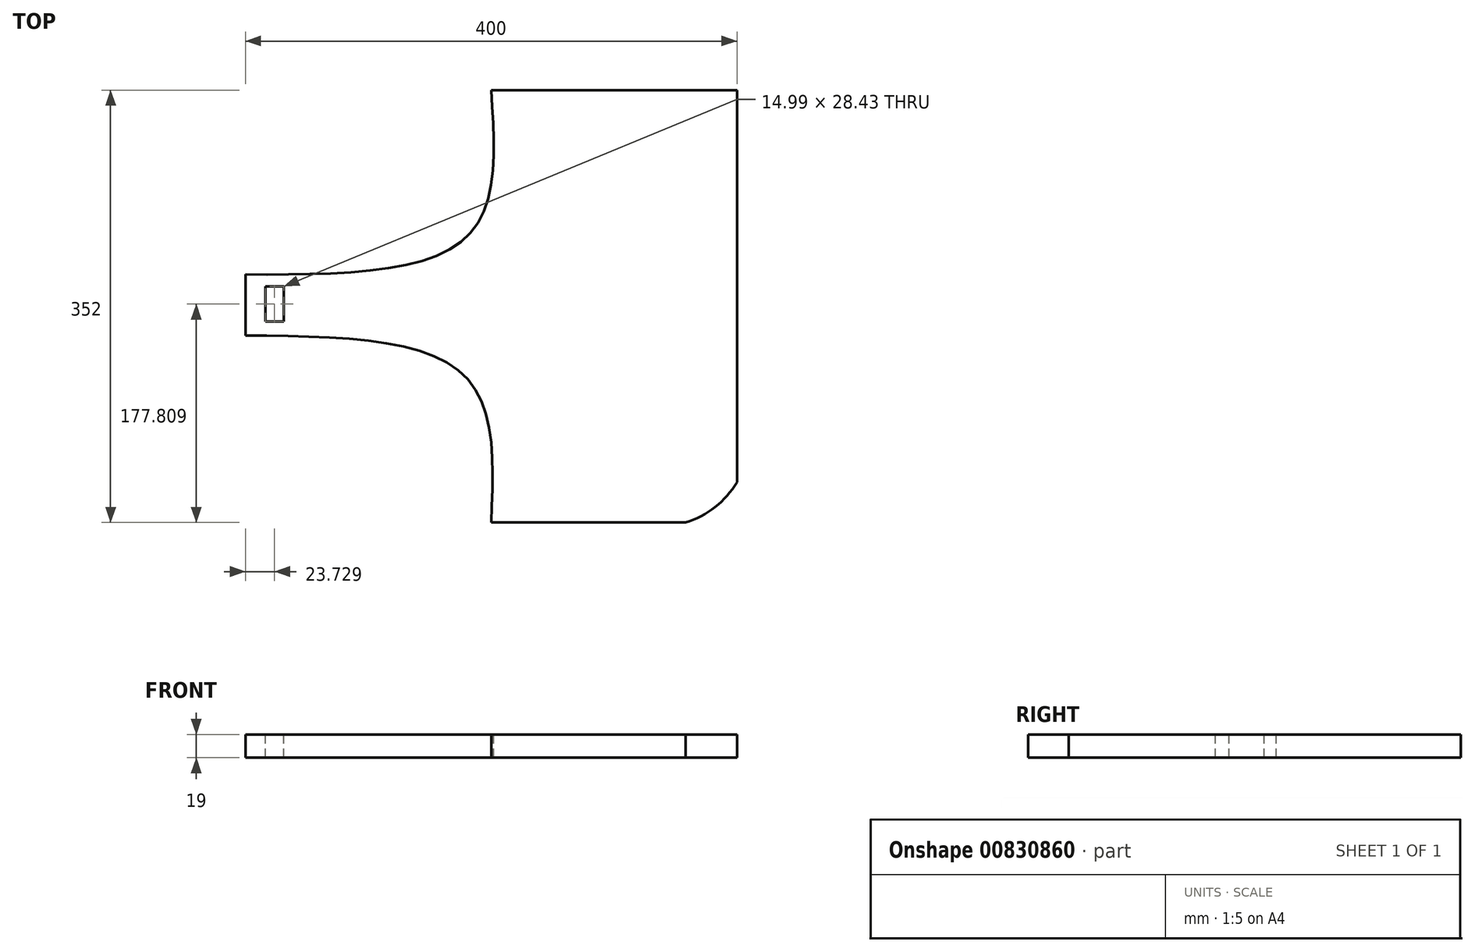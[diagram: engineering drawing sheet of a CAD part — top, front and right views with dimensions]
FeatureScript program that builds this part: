
annotation { "Feature Type Name" : "Feature", "Feature Type Description" : "" }
export const myFeature = defineFeature(function(context is Context, id is Id, definition is map)
    precondition{}
    {
        {
            var Q0;
            Q0=qCreatedBy(makeId("Top.planeOp"),FACE);
            var sketch = newSketch(context, id + "F0", { "sketchPlane" : qUnion([Q0])});
            skLineSegment(sketch, "E0.bottom", {"start": v(200, -176) * mm, "end": v(-200, -176) * mm});
            skLineSegment(sketch, "E0.top", {"start": v(200, 176) * mm, "end": v(-200, 176) * mm});
            skLineSegment(sketch, "E0.left", {"start": v(200, -176) * mm, "end": v(200, 176) * mm});
            skLineSegment(sketch, "E0.right", {"start": v(-200, -176) * mm, "end": v(-200, 176) * mm});
            skPoint(sketch, "E0.middle", {"position": v(0, 0) * mm});
            skSolve(sketch);
        }
        {
            var Q0;
            Q0=makeQuery(id+"F0.imprint","IMPRINT",FACE,{"disambiguationData":[TD([[makeQuery(id+"F0.imprint","IMPRINT",EDGE,{"derivedFrom":sQuery(id+"F0.wireOp",EDGE,"E0.bottom")}),-1.0]])]});
            extrude(context, id + "F1", {"entities" : qUnion([Q0]), "depth" : 19 * mm, "offsetDistance" : 25 * mm});
        }
        {
            var Q0;
            Q0=makeQuery(id+"F1.opExtrude","CAP_FACE",FACE,{"disambiguationData":[OSD([sQuery(id+"F0.wireOp",EDGE,"E0.bottom"),sQuery(id+"F0.wireOp",EDGE,"E0.top"),sQuery(id+"F0.wireOp",EDGE,"E0.left"),sQuery(id+"F0.wireOp",EDGE,"E0.right")])],"isStart":false});
            var sketch = newSketch(context, id + "F2", { "sketchPlane" : qUnion([Q0])});
            skFitSpline(sketch, "E1", {"points": [v(-200, -23.78) * mm, v(-21.45, -56.86) * mm, v(0, -176) * mm], "startDerivative": vector(400.47, -3.68) * mm, "endDerivative": vector(-14.44, -311.12) * mm});
            skFitSpline(sketch, "E2", {"points": [v(-200, 25.85) * mm, v(-18.87, 57.38) * mm, v(0, 176) * mm], "startDerivative": vector(406.43, -0.6) * mm, "endDerivative": vector(-21.56, 311.95) * mm});
            skLineSegment(sketch, "E3.bottom", {"start": v(-177.27, 14.17) * mm, "end": v(-156.69, 14.17) * mm});
            skLineSegment(sketch, "E3.top", {"start": v(-177.27, -14.17) * mm, "end": v(-156.69, -14.17) * mm});
            skLineSegment(sketch, "E3.left", {"start": v(-177.27, 14.17) * mm, "end": v(-177.27, -14.17) * mm});
            skLineSegment(sketch, "E3.right", {"start": v(-156.69, 14.17) * mm, "end": v(-156.69, -14.17) * mm});
            skPoint(sketch, "E3.middle", {"position": v(-166.98, 0) * mm});
            skSolve(sketch);
        }
        {
            var Q0;
            {var subQ0=sQuery(id+"F2.wireOp",EDGE,"E1");Q0=makeQuery(id+"F2.imprint","IMPRINT",FACE,{"disambiguationData":[TD([[makeQuery(id+"F2.imprint","IMPRINT",EDGE,{"derivedFrom":subQ0}),-1.0]])]});}
            var Q1;
            {var subQ0=sQuery(id+"F2.wireOp",EDGE,"E2");Q1=makeQuery(id+"F2.imprint","IMPRINT",FACE,{"disambiguationData":[TD([[makeQuery(id+"F2.imprint","IMPRINT",EDGE,{"derivedFrom":subQ0}),1.0]])]});}
            extrude(context, id + "F3", {"entities" : qUnion([Q0, Q1]), "operationType" : NewBodyOperationType.REMOVE, "endBound" : BoundingType.THROUGH_ALL, "oppositeDirection" : true, "depth" : 25 * mm, "offsetDistance" : 25 * mm});
        }
        {
            var Q0;
            Q0=makeQuery(id+"F1.opExtrude","CAP_FACE",FACE,{"disambiguationData":[OSD([sQuery(id+"F0.wireOp",EDGE,"E0.bottom"),sQuery(id+"F0.wireOp",EDGE,"E0.top"),sQuery(id+"F0.wireOp",EDGE,"E0.left"),sQuery(id+"F0.wireOp",EDGE,"E0.right")])],"isStart":false});
            var sketch = newSketch(context, id + "F4", { "sketchPlane" : qUnion([Q0])});
            skArc(sketch, "E4", {"start": v(158.15, -176) * mm, "mid": v(182.18, -163.53) * mm, "end": v(200, -143.15) * mm});
            skArc(sketch, "E5", {"start": v(200, 146.27) * mm, "mid": v(188.48, 170.49) * mm, "end": v(162.23, 176) * mm});
            skArc(sketch, "E6", {"start": v(0.88, -155.04) * mm, "mid": v(6.69, -169.96) * mm, "end": v(21.51, -176) * mm});
            skArc(sketch, "E7", {"start": v(21.51, 176) * mm, "mid": v(5.92, 172.28) * mm, "end": v(1.25, 156.95) * mm});
            skSolve(sketch);
        }
        {
            var Q0;
            {var subQ0=sQuery(id+"F4.wireOp",EDGE,"E5");var subQ1=makeQuery(id+"F1.opExtrude","CAP_EDGE",EDGE,{"disambiguationData":[OSD([sQuery(id+"F0.wireOp",EDGE,"E0.left")])],"isStart":false});var subQ2=makeQuery(id+"F4.imprint","INTERSECT",VERTEX,{"disambiguationData":[OD(1.0)],"derivedFrom":[subQ1,subQ0]});Q0=makeQuery(id+"F4.imprint","IMPRINT",FACE,{"disambiguationData":[TD([[makeQuery(id+"F4.imprint","IMPRINT",EDGE,{"disambiguationData":[TD([[subQ2,-1.0]])],"derivedFrom":subQ0}),-1.0]])]});}
            var Q1;
            {var subQ0=sQuery(id+"F4.wireOp",EDGE,"E4");Q1=makeQuery(id+"F4.imprint","IMPRINT",FACE,{"disambiguationData":[TD([[makeQuery(id+"F4.imprint","IMPRINT",EDGE,{"derivedFrom":subQ0}),-1.0]])]});}
            extrude(context, id + "F5", {"entities" : qUnion([Q0, Q1]), "operationType" : NewBodyOperationType.REMOVE, "endBound" : BoundingType.THROUGH_ALL, "oppositeDirection" : true, "depth" : 25 * mm, "offsetDistance" : 25 * mm});
        }
        {
            var Q0;
            Q0=makeQuery(id+"F1.opExtrude","CAP_FACE",FACE,{"disambiguationData":[OSD([sQuery(id+"F0.wireOp",EDGE,"E0.bottom"),sQuery(id+"F0.wireOp",EDGE,"E0.top"),sQuery(id+"F0.wireOp",EDGE,"E0.left"),sQuery(id+"F0.wireOp",EDGE,"E0.right")])],"isStart":false});
            var sketch = newSketch(context, id + "F6", { "sketchPlane" : qUnion([Q0])});
            skLineSegment(sketch, "E8.bottom", {"start": v(-183.77, 16.02) * mm, "end": v(-168.78, 16.02) * mm});
            skLineSegment(sketch, "E8.top", {"start": v(-183.77, -12.4) * mm, "end": v(-168.78, -12.4) * mm});
            skLineSegment(sketch, "E8.left", {"start": v(-183.77, 16.02) * mm, "end": v(-183.77, -12.4) * mm});
            skLineSegment(sketch, "E8.right", {"start": v(-168.78, 16.02) * mm, "end": v(-168.78, -12.4) * mm});
            skSolve(sketch);
        }
        {
            var Q0;
            Q0=makeQuery(id+"F6.imprint","IMPRINT",FACE,{"disambiguationData":[TD([[makeQuery(id+"F6.imprint","IMPRINT",EDGE,{"derivedFrom":sQuery(id+"F6.wireOp",EDGE,"E8.bottom")}),-1.0]])]});
            extrude(context, id + "F7", {"entities" : qUnion([Q0]), "operationType" : NewBodyOperationType.REMOVE, "endBound" : BoundingType.THROUGH_ALL, "oppositeDirection" : true, "depth" : 25 * mm, "offsetDistance" : 25 * mm});
        }
    });
